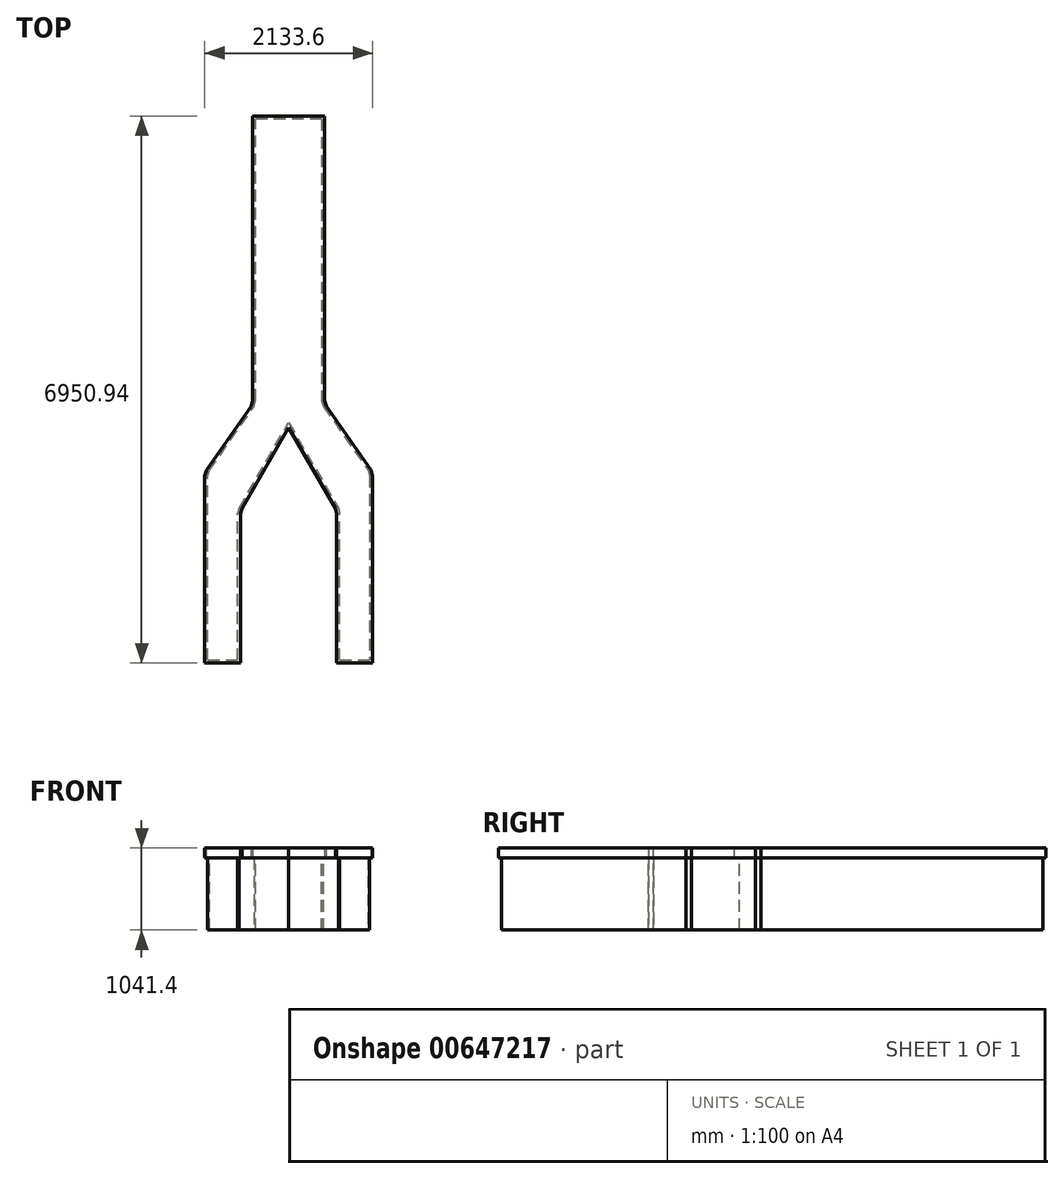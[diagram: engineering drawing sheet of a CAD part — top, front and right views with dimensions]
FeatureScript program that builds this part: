
annotation { "Feature Type Name" : "Feature", "Feature Type Description" : "" }
export const myFeature = defineFeature(function(context is Context, id is Id, definition is map)
    precondition{}
    {
        {
            var Q0;
            Q0=qCreatedBy(makeId("Top.planeOp"),FACE);
            var sketch = newSketch(context, id + "F0", { "sketchPlane" : qUnion([Q0])});
            skLineSegment(sketch, "E0.bottom", {"start": v(0, 0) * mm, "end": v(-457.2, 0) * mm});
            skLineSegment(sketch, "E0.left", {"start": v(0, 0) * mm, "end": v(0, 1934.9) * mm});
            skLineSegment(sketch, "E1", {"start": v(0, 1934.9) * mm, "end": v(609.6, 2990.76) * mm});
            skLineSegment(sketch, "E2", {"start": v(152.4, 3293.34) * mm, "end": v(-457.2, 2417.87) * mm});
            skLineSegment(sketch, "E3", {"start": v(-457.2, 2417.87) * mm, "end": v(-457.2, 0) * mm});
            skLineSegment(sketch, "E4.MirrorCS", {"start": v(1066.8, 3293.34) * mm, "end": v(1676.4, 2417.87) * mm});
            skLineSegment(sketch, "E5.MirrorCS", {"start": v(1676.4, 2417.87) * mm, "end": v(1676.4, 0) * mm});
            skLineSegment(sketch, "E6.MirrorCS", {"start": v(1219.2, 0) * mm, "end": v(1219.2, 1934.9) * mm});
            skLineSegment(sketch, "E7", {"start": v(1219.2, 0) * mm, "end": v(1676.4, 0) * mm});
            skLineSegment(sketch, "E8", {"start": v(1219.2, 1934.9) * mm, "end": v(609.6, 2990.76) * mm});
            skLineSegment(sketch, "E9.top", {"start": v(1066.8, 6950.94) * mm, "end": v(152.4, 6950.94) * mm});
            skLineSegment(sketch, "E9.left", {"start": v(1066.8, 3293.34) * mm, "end": v(1066.8, 6950.94) * mm});
            skLineSegment(sketch, "E9.right", {"start": v(152.4, 3293.34) * mm, "end": v(152.4, 6950.94) * mm});
            skSolve(sketch);
        }
        {
            var Q0;
            Q0 = qSketchRegion(id + "F0", true);
            extrude(context, id + "F1", {"entities" : qUnion([Q0]), "depth" : 127 * mm, "offsetDistance" : 25.4 * mm});
        }
        {
            var Q0;
            Q0=makeQuery(id+"F1.opExtrude","CAP_FACE",FACE,{"disambiguationData":[OSD([sQuery(id+"F0.wireOp",EDGE,"E0.bottom"),sQuery(id+"F0.wireOp",EDGE,"E0.left"),sQuery(id+"F0.wireOp",EDGE,"E1"),sQuery(id+"F0.wireOp",EDGE,"iZg9pOZI-lDCc-dJxI-UXmY-ILLoGJ9nuKQN"),sQuery(id+"F0.wireOp",EDGE,"E2"),sQuery(id+"F0.wireOp",EDGE,"E3"),sQuery(id+"F0.wireOp",EDGE,"40b35680-ef71-4b77-a404-9541dbc10bcf0.MirrorCS"),sQuery(id+"F0.wireOp",EDGE,"07cf3ead-9002-4f03-bed2-3ebd035167170.MirrorCS"),sQuery(id+"F0.wireOp",EDGE,"E4.MirrorCS"),sQuery(id+"F0.wireOp",EDGE,"E5.MirrorCS"),sQuery(id+"F0.wireOp",EDGE,"E6.MirrorCS"),sQuery(id+"F0.wireOp",EDGE,"f6f09d63-dda0-45c4-8892-0b64a1d0b5190.MirrorCS"),sQuery(id+"F0.wireOp",EDGE,"rIIMSqh5-YHhh-YraX-uaZf-FADusHcue9YW")])],"isStart":true});
            var sketch = newSketch(context, id + "F2", { "sketchPlane" : qUnion([Q0])});
            skPoint(sketch, "E10", {"position": v(-419.1, 0) * mm});
            skPoint(sketch, "E11", {"position": v(-38.1, 0) * mm});
            skPoint(sketch, "E12", {"position": v(1219.2, 0) * mm});
            skPoint(sketch, "E13", {"position": v(1676.4, -2417.87) * mm});
            skPoint(sketch, "E14", {"position": v(1257.34, -1934.93) * mm});
            skPoint(sketch, "E15", {"position": v(1219.2, -38.1) * mm});
            skPoint(sketch, "E16", {"position": v(0, -38.1) * mm});
            skPoint(sketch, "E17", {"position": v(-457.2, -38.1) * mm});
            skPoint(sketch, "E18", {"position": v(1676.4, -2455.97) * mm});
            skLineSegment(sketch, "E19", {"start": v(-419.1, -38.1) * mm, "end": v(-38.1, -38.1) * mm});
            skLineSegment(sketch, "E20", {"start": v(-38.1, -38.1) * mm, "end": v(-38.1, -1934.9) * mm});
            skLineSegment(sketch, "E21", {"start": v(-38.1, -1934.9) * mm, "end": v(609.6, -3056.76) * mm});
            skPoint(sketch, "E22", {"position": v(-419.1, -2417.87) * mm});
            skLineSegment(sketch, "E23", {"start": v(-419.1, -38.1) * mm, "end": v(-419.1, -2417.87) * mm});
            skLineSegment(sketch, "E24", {"start": v(1257.3, -38.1) * mm, "end": v(1257.34, -1934.93) * mm});
            skLineSegment(sketch, "E25", {"start": v(609.6, -3056.76) * mm, "end": v(1257.34, -1934.93) * mm});
            skPoint(sketch, "E26", {"position": v(190.5, -3293.34) * mm});
            skPoint(sketch, "E27", {"position": v(1028.7, -3293.34) * mm});
            skLineSegment(sketch, "E28", {"start": v(190.5, -3293.34) * mm, "end": v(190.5, -6912.84) * mm});
            skLineSegment(sketch, "E29", {"start": v(1028.7, -6912.84) * mm, "end": v(1028.7, -3293.34) * mm});
            skLineSegment(sketch, "E30", {"start": v(1028.7, -3293.34) * mm, "end": v(1638.3, -2417.87) * mm});
            skLineSegment(sketch, "E31", {"start": v(-419.1, -2417.87) * mm, "end": v(190.5, -3293.34) * mm});
            skPoint(sketch, "E32", {"position": v(1638.3, -38.1) * mm});
            skLineSegment(sketch, "E33", {"start": v(1257.3, -38.1) * mm, "end": v(1638.3, -38.1) * mm});
            skLineSegment(sketch, "E34", {"start": v(1638.3, -2417.87) * mm, "end": v(1638.3, -38.1) * mm});
            skLineSegment(sketch, "E35", {"start": v(1028.7, -6912.84) * mm, "end": v(190.5, -6912.84) * mm});
            skSolve(sketch);
        }
        {
            var Q0;
            Q0 = qSketchRegion(id + "F2", true);
            extrude(context, id + "F3", {"entities" : qUnion([Q0]), "operationType" : NewBodyOperationType.ADD, "depth" : 914.4 * mm, "offsetDistance" : 25.4 * mm});
        }
        {
            var Q0;
            Q0=makeQuery(id+"F3.opExtrude","SWEPT_EDGE",EDGE,{"disambiguationData":[OSD([sQuery(id+"F2.wireOp",EDGE,"E30"),sQuery(id+"F2.wireOp",EDGE,"E34")])]});
            var Q1;
            Q1=makeQuery(id+"F3.opExtrude","SWEPT_EDGE",EDGE,{"disambiguationData":[OSD([sQuery(id+"F2.wireOp",EDGE,"E23"),sQuery(id+"F2.wireOp",EDGE,"E31")])]});
            var Q2;
            Q2=makeQuery(id+"F3.opExtrude","SWEPT_EDGE",EDGE,{"disambiguationData":[OSD([sQuery(id+"F2.wireOp",EDGE,"E24"),sQuery(id+"F2.wireOp",EDGE,"E25")])]});
            var Q3;
            Q3=makeQuery(id+"F3.opExtrude","SWEPT_EDGE",EDGE,{"disambiguationData":[OSD([sQuery(id+"F2.wireOp",EDGE,"E20"),sQuery(id+"F2.wireOp",EDGE,"E21")])]});
            var Q4;
            Q4=makeQuery(id+"F1.opExtrude","SWEPT_EDGE",EDGE,{"disambiguationData":[OSD([sQuery(id+"F0.wireOp",EDGE,"E0.left"),sQuery(id+"F0.wireOp",EDGE,"E1")])]});
            var Q5;
            Q5=makeQuery(id+"F1.opExtrude","SWEPT_EDGE",EDGE,{"disambiguationData":[OSD([sQuery(id+"F0.wireOp",EDGE,"E4.MirrorCS"),sQuery(id+"F0.wireOp",EDGE,"Au21ltp3-rCSn-RR8l-7Xuw-KehPPDg3waVN")])]});
            var Q6;
            Q6=makeQuery(id+"F1.opExtrude","SWEPT_EDGE",EDGE,{"disambiguationData":[OSD([sQuery(id+"F0.wireOp",EDGE,"E4.MirrorCS"),sQuery(id+"F0.wireOp",EDGE,"E5.MirrorCS")])]});
            var Q7;
            Q7=makeQuery(id+"F3.opExtrude","SWEPT_EDGE",EDGE,{"disambiguationData":[OSD([sQuery(id+"F2.wireOp",EDGE,"E29"),sQuery(id+"F2.wireOp",EDGE,"E30")])]});
            var Q8;
            Q8=makeQuery(id+"F1.opExtrude","SWEPT_EDGE",EDGE,{"disambiguationData":[OSD([sQuery(id+"F0.wireOp",EDGE,"E6.MirrorCS"),sQuery(id+"F0.wireOp",EDGE,"E8")])]});
            var Q9;
            Q9=makeQuery(id+"F1.opExtrude","SWEPT_EDGE",EDGE,{"disambiguationData":[OSD([sQuery(id+"F0.wireOp",EDGE,"E2"),sQuery(id+"F0.wireOp",EDGE,"E3")])]});
            var Q10;
            Q10=makeQuery(id+"F1.opExtrude","SWEPT_EDGE",EDGE,{"disambiguationData":[OSD([sQuery(id+"F0.wireOp",EDGE,"E2"),sQuery(id+"F0.wireOp",EDGE,"N4cl1NMr-r29l-sN2G-F0GU-56zY6LMfHCqh")])]});
            var Q11;
            Q11=makeQuery(id+"F3.opExtrude","SWEPT_EDGE",EDGE,{"disambiguationData":[OSD([sQuery(id+"F2.wireOp",EDGE,"E28"),sQuery(id+"F2.wireOp",EDGE,"E31")])]});
            chamfer(context, id + "F4", {"entities" : qUnion([Q0, Q1, Q2, Q3, Q4, Q5, Q6, Q7, Q8, Q9, Q10, Q11]), "width" : 127 * mm, "tangentPropagation" : true});
        }
    });
